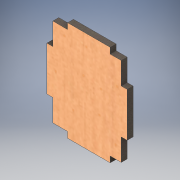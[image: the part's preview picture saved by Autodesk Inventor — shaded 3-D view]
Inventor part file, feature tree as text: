
AUTODESK INVENTOR PART (.ipt)
format: ipt  version: 2019 (Build 230136000, 136)  size: 138,240 bytes
history: native  units: mm
features: other x1, extrude x1, sketch x1
ambient origin geometry x8: Origin, YZ Plane, XZ Plane, XY Plane, X Axis, Y Axis, Z Axis, Center Point
bodies: Body1 (feature_tree)
feature tree (3):
  other  "Твердое тело1"
  extrude  "Выдавливание1"  Depth=29.0mm
  sketch  "Эскиз1"
